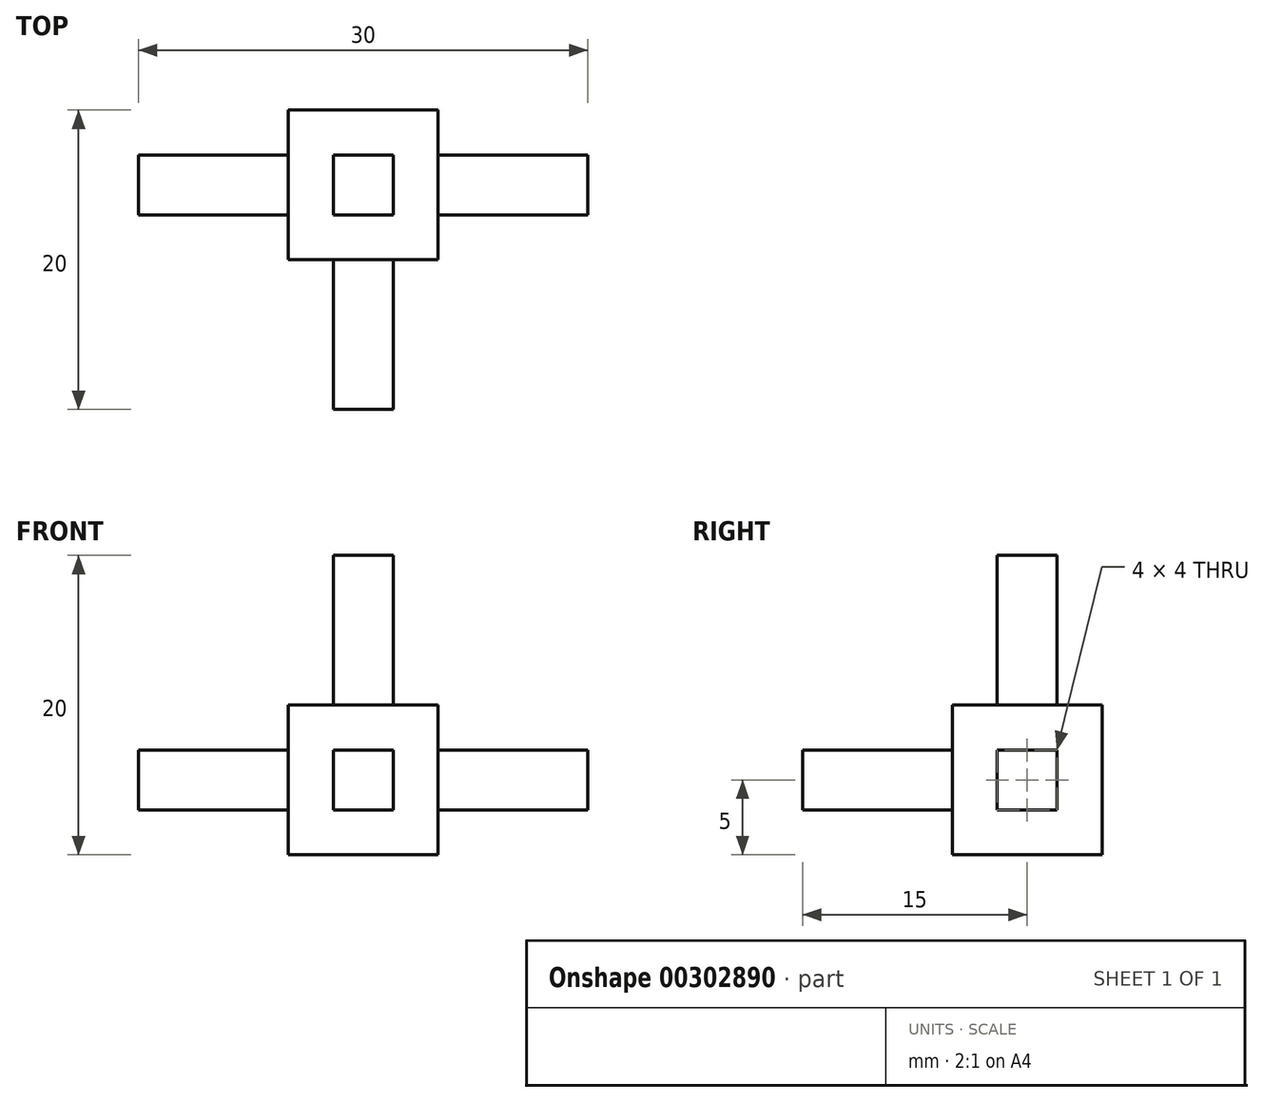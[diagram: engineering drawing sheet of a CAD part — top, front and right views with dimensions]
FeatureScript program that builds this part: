
annotation { "Feature Type Name" : "Feature", "Feature Type Description" : "" }
export const myFeature = defineFeature(function(context is Context, id is Id, definition is map)
    precondition{}
    {
        {
            var Q0;
            Q0=qCreatedBy(makeId("Top.planeOp"),FACE);
            var sketch = newSketch(context, id + "F0", { "sketchPlane" : qUnion([Q0])});
            skLineSegment(sketch, "E0.bottom", {"start": v(-5, 5) * mm, "end": v(5, 5) * mm});
            skLineSegment(sketch, "E0.top", {"start": v(-5, -5) * mm, "end": v(5, -5) * mm});
            skLineSegment(sketch, "E0.left", {"start": v(-5, 5) * mm, "end": v(-5, -5) * mm});
            skLineSegment(sketch, "E0.right", {"start": v(5, 5) * mm, "end": v(5, -5) * mm});
            skPoint(sketch, "E0.middle", {"position": v(0, 0) * mm});
            skSolve(sketch);
        }
        {
            var Q0;
            Q0=qSketchRegion(id+"F0",true);
            extrude(context, id + "F1", {"entities" : qUnion([Q0]), "endBound" : BoundingType.SYMMETRIC, "depth" : 10 * mm});
        }
        {
            var Q0;
            Q0=qCreatedBy(makeId("Top.planeOp"),FACE);
            var sketch = newSketch(context, id + "F2", { "sketchPlane" : qUnion([Q0])});
            skLineSegment(sketch, "E1.bottom", {"start": v(-2, 2) * mm, "end": v(2, 2) * mm});
            skLineSegment(sketch, "E1.top", {"start": v(-2, -2) * mm, "end": v(2, -2) * mm});
            skLineSegment(sketch, "E1.left", {"start": v(-2, 2) * mm, "end": v(-2, -2) * mm});
            skLineSegment(sketch, "E1.right", {"start": v(2, 2) * mm, "end": v(2, -2) * mm});
            skPoint(sketch, "E1.middle", {"position": v(0, 0) * mm});
            skSolve(sketch);
        }
        {
            var Q0;
            Q0=qSketchRegion(id+"F2",true);
            extrude(context, id + "F3", {"entities" : qUnion([Q0]), "operationType" : NewBodyOperationType.ADD, "depth" : 15 * mm});
        }
        {
            var Q0;
            Q0=qCreatedBy(makeId("Front.planeOp"),FACE);
            var sketch = newSketch(context, id + "F4", { "sketchPlane" : qUnion([Q0])});
            skLineSegment(sketch, "E2.bottom", {"start": v(2, 2) * mm, "end": v(-2, 2) * mm});
            skLineSegment(sketch, "E2.top", {"start": v(2, -2) * mm, "end": v(-2, -2) * mm});
            skLineSegment(sketch, "E2.left", {"start": v(2, 2) * mm, "end": v(2, -2) * mm});
            skLineSegment(sketch, "E2.right", {"start": v(-2, 2) * mm, "end": v(-2, -2) * mm});
            skPoint(sketch, "E2.middle", {"position": v(0, 0) * mm});
            skSolve(sketch);
        }
        {
            var Q0;
            Q0=qSketchRegion(id+"F4",true);
            extrude(context, id + "F5", {"entities" : qUnion([Q0]), "operationType" : NewBodyOperationType.ADD, "depth" : 15 * mm});
        }
        {
            var Q0;
            Q0=qCreatedBy(makeId("Right.planeOp"),FACE);
            var sketch = newSketch(context, id + "F6", { "sketchPlane" : qUnion([Q0])});
            skLineSegment(sketch, "E3.bottom", {"start": v(-2, 2) * mm, "end": v(2, 2) * mm});
            skLineSegment(sketch, "E3.top", {"start": v(-2, -2) * mm, "end": v(2, -2) * mm});
            skLineSegment(sketch, "E3.left", {"start": v(-2, 2) * mm, "end": v(-2, -2) * mm});
            skLineSegment(sketch, "E3.right", {"start": v(2, 2) * mm, "end": v(2, -2) * mm});
            skPoint(sketch, "E3.middle", {"position": v(0, 0) * mm});
            skSolve(sketch);
        }
        {
            var Q0;
            Q0=qSketchRegion(id+"F6",true);
            extrude(context, id + "F7", {"entities" : qUnion([Q0]), "operationType" : NewBodyOperationType.ADD, "depth" : 15 * mm});
        }
        {
            var Q0;
            Q0 = qSketchRegion(id + "F6", true);
            extrude(context, id + "F8", {"entities" : qUnion([Q0]), "operationType" : NewBodyOperationType.ADD, "oppositeDirection" : true, "depth" : 15 * mm});
        }
    });
